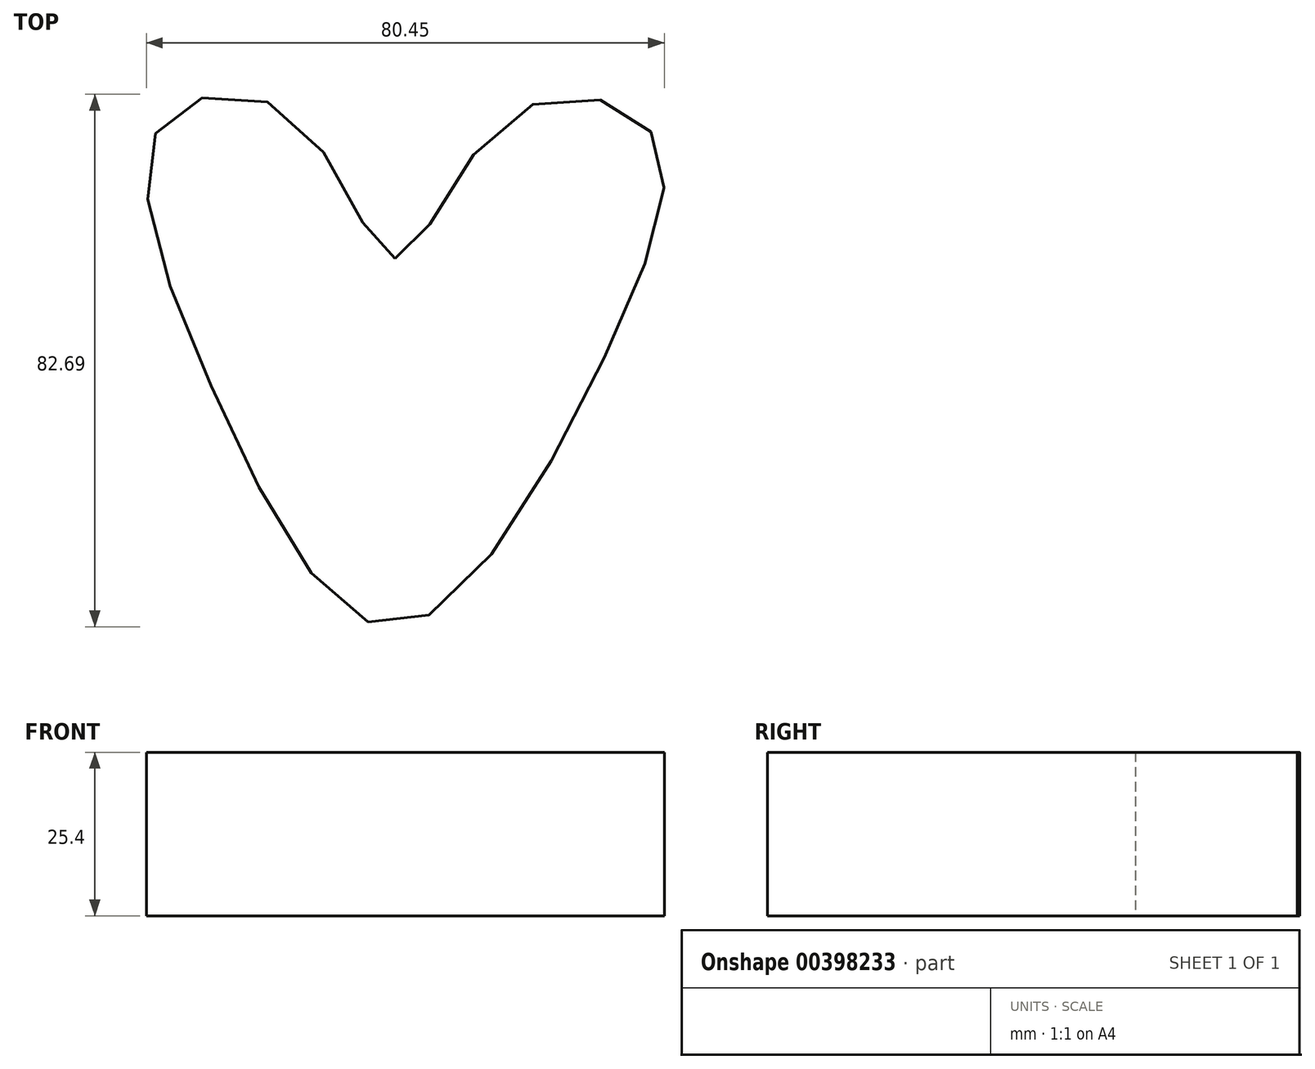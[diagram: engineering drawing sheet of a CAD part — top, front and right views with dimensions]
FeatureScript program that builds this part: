
annotation { "Feature Type Name" : "Feature", "Feature Type Description" : "" }
export const myFeature = defineFeature(function(context is Context, id is Id, definition is map)
    precondition{}
    {
        {
            var Q0;
            Q0=qCreatedBy(makeId("Top.planeOp"),FACE);
            var sketch = newSketch(context, id + "F0", { "sketchPlane" : qUnion([Q0])});
            skPoint(sketch, "E0.3.internal.orphan", {"position": v(54.28, 0) * mm});
            skPoint(sketch, "E0.4.internal.orphan", {"position": v(0, -57.15) * mm});
            skFitSpline(sketch, "E1", {"points": [v(0, 0) * mm, v(17.78, 22) * mm, v(39.55, 19.94) * mm, v(33.62, -12.87) * mm, v(0, -57.15) * mm, v(-27.85, -21.43) * mm, v(-36.5, 20.59) * mm, v(-15.9, 22) * mm, v(0, 0) * mm]});
            skSolve(sketch);
        }
        {
            var Q0;
            Q0 = qSketchRegion(id + "F0", true);
            extrude(context, id + "F1", {"entities" : qUnion([Q0]), "depth" : 25.4 * mm});
        }
    });
